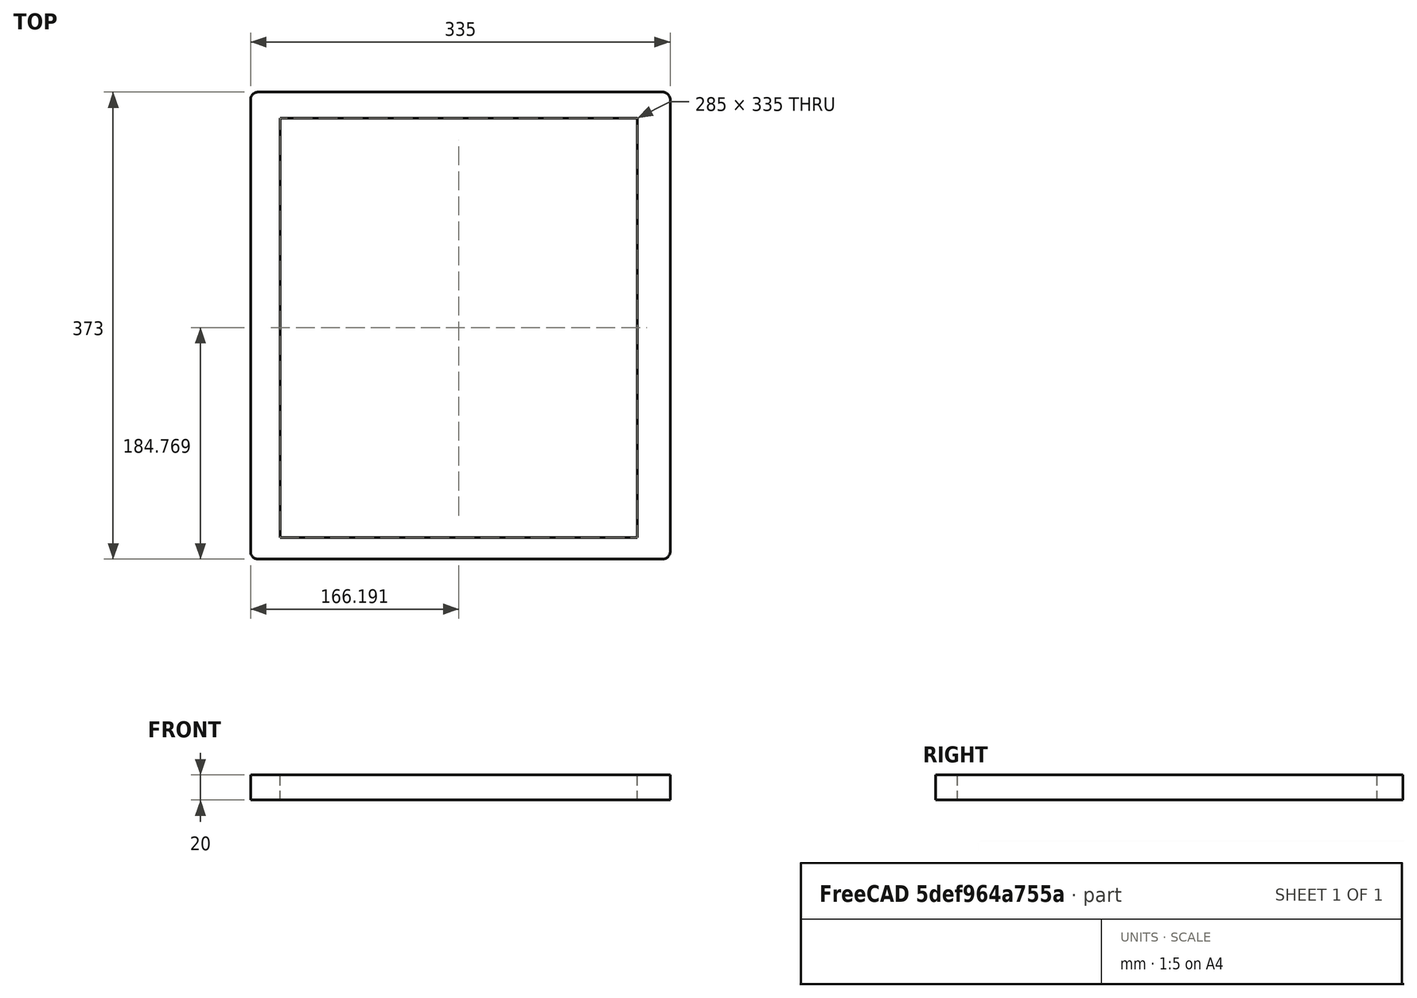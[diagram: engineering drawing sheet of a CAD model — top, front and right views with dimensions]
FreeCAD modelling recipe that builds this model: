
FCSTD DOCUMENT  (FreeCAD 0.16R6706 (Git))
Label: back
License: All rights reserved
LicenseURL: http://en.wikipedia.org/wiki/All_rights_reserved
objects: Sketcher::SketchObject×1, PartDesign::Pad×1
note: 3 computed .brp shape members not serialized (recipe doc carries the construction recipe); baked Part::Feature solids carry a one-line shape summary decoded from their .brp

FEATURE [Sketcher::SketchObject] Sketch
  sketch-geometry (12):
    g0: LineSegment StartX=-174.643 StartY=156.977 StartZ=0 EndX=148.357 EndY=156.977 EndZ=0
    g1: LineSegment StartX=154.357 StartY=150.977 StartZ=0 EndX=154.357 EndY=-210.023 EndZ=0
    g2: LineSegment StartX=148.357 StartY=-216.023 StartZ=0 EndX=-174.643 EndY=-216.023 EndZ=0
    g3: LineSegment StartX=-180.643 StartY=-210.023 StartZ=0 EndX=-180.643 EndY=150.977 EndZ=0
    g4: ArcOfCircle CenterX=-174.643 CenterY=150.977 CenterZ=0 NormalX=0 NormalY=0 NormalZ=1 Radius=6 StartAngle=1.5708 EndAngle=3.14159
    g5: ArcOfCircle CenterX=148.357 CenterY=150.977 CenterZ=0 NormalX=0 NormalY=0 NormalZ=1 Radius=6 StartAngle=0 EndAngle=1.5708
    g6: ArcOfCircle CenterX=148.357 CenterY=-210.023 CenterZ=0 NormalX=0 NormalY=0 NormalZ=1 Radius=6 StartAngle=4.71239 EndAngle=6.28319
    g7: ArcOfCircle CenterX=-174.643 CenterY=-210.023 CenterZ=0 NormalX=0 NormalY=0 NormalZ=1 Radius=6 StartAngle=3.14159 EndAngle=4.71239
    g8: LineSegment StartX=-156.949 StartY=136.249 StartZ=0 EndX=128.051 EndY=136.249 EndZ=0
    g9: LineSegment StartX=128.051 StartY=136.249 StartZ=0 EndX=128.051 EndY=-198.751 EndZ=0
    g10: LineSegment StartX=128.051 StartY=-198.751 StartZ=0 EndX=-156.949 EndY=-198.751 EndZ=0
    g11: LineSegment StartX=-156.949 StartY=-198.751 StartZ=0 EndX=-156.949 EndY=136.249 EndZ=0
  constraints (28):
    c: Horizontal(g0)
    c: Horizontal(g2)
    c: Vertical(g1)
    c: Vertical(g3)
    c: Tangent(g3,g4) = 1.5708
    c: Tangent(g0,g4) = 1.5708
    c: Tangent(g0,g5) = 1.5708
    c: Tangent(g1,g5) = 1.5708
    c: Tangent(g1,g6) = 1.5708
    c: Tangent(g2,g6) = 1.5708
    c: Tangent(g2,g7) = 1.5708
    c: Tangent(g3,g7) = 1.5708
    c: Radius(g4) = 6
    c: Equal(g4,g5)
    c: Equal(g4,g6)
    c: Equal(g4,g7)
    c: Distance(g3,g1) = 335
    c: Distance(g0,g2) = 373
    c: Coincident(g8,g9)
    c: Coincident(g9,g10)
    c: Coincident(g10,g11)
    c: Coincident(g11,g8)
    c: Horizontal(g8)
    c: Horizontal(g10)
    c: Vertical(g9)
    c: Vertical(g11)
    c: DistanceX(g8,g8) = 285
    c: DistanceY(g9,g9) = 335
FEATURE [PartDesign::Pad] Pad
  Length = 20
  Length2 = 100
  Sketch = -> Sketch
  Type = 0
